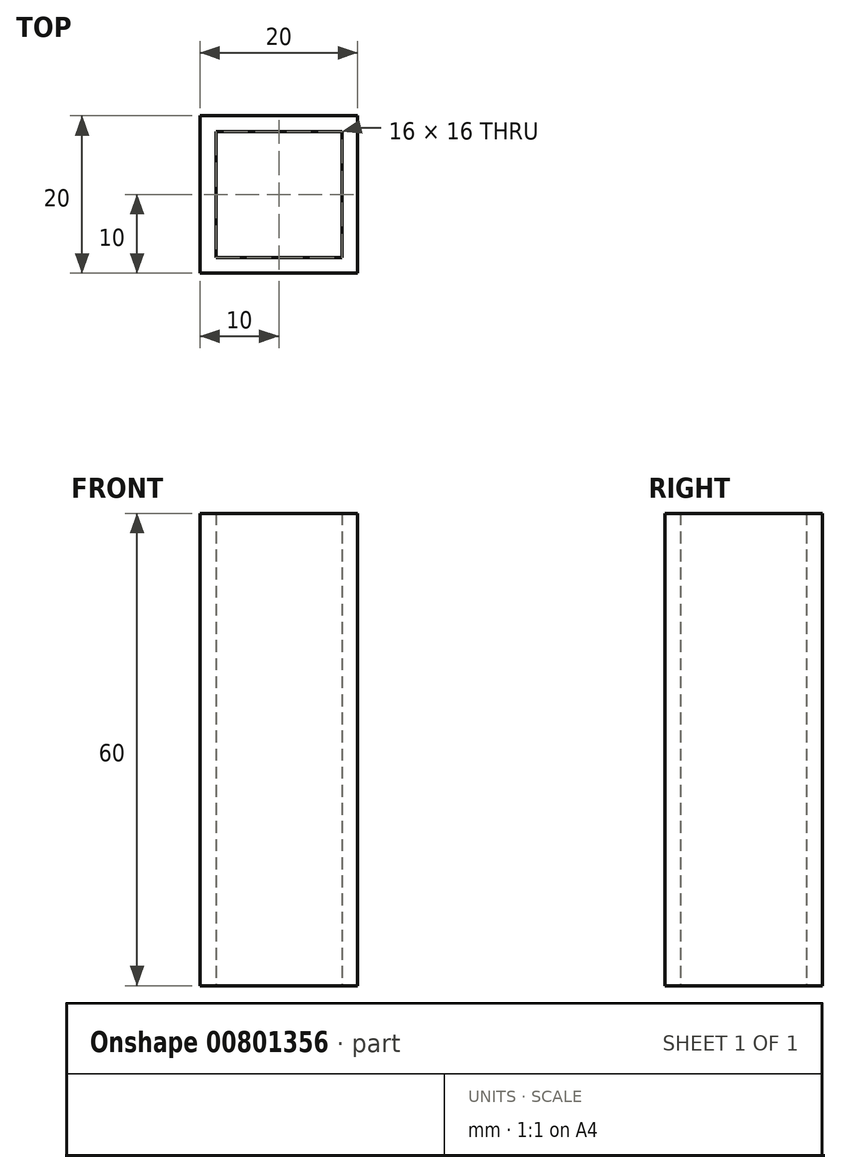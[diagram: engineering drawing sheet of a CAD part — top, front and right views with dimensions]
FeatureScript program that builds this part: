
annotation { "Feature Type Name" : "Feature", "Feature Type Description" : "" }
export const myFeature = defineFeature(function(context is Context, id is Id, definition is map)
    precondition{}
    {
        {
            var Q0;
            Q0=qCreatedBy(makeId("Top.planeOp"),FACE);
            var sketch = newSketch(context, id + "F0", { "sketchPlane" : qUnion([Q0])});
            skLineSegment(sketch, "E0.bottom", {"start": v(10, 10) * mm, "end": v(-10, 10) * mm});
            skLineSegment(sketch, "E0.top", {"start": v(10, -10) * mm, "end": v(-10, -10) * mm});
            skLineSegment(sketch, "E0.left", {"start": v(10, 10) * mm, "end": v(10, -10) * mm});
            skLineSegment(sketch, "E0.right", {"start": v(-10, 10) * mm, "end": v(-10, -10) * mm});
            skPoint(sketch, "E0.middle", {"position": v(0, 0) * mm});
            skLineSegment(sketch, "E1.0", {"start": v(8, 8) * mm, "end": v(-8, 8) * mm});
            skLineSegment(sketch, "E1.1", {"start": v(8, 8) * mm, "end": v(8, -8) * mm});
            skLineSegment(sketch, "E1.2", {"start": v(8, -8) * mm, "end": v(-8, -8) * mm});
            skLineSegment(sketch, "E1.3", {"start": v(-8, 8) * mm, "end": v(-8, -8) * mm});
            skSolve(sketch);
        }
        {
            var Q0;
            Q0=makeQuery(id+"F0.imprint","IMPRINT",FACE,{"disambiguationData":[TD([[makeQuery(id+"F0.imprint","IMPRINT",EDGE,{"derivedFrom":sQuery(id+"F0.wireOp",EDGE,"E0.bottom")}),1.0]])]});
            extrude(context, id + "F1", {"entities" : qUnion([Q0]), "depth" : 60 * mm, "offsetDistance" : 25 * mm});
        }
    });
